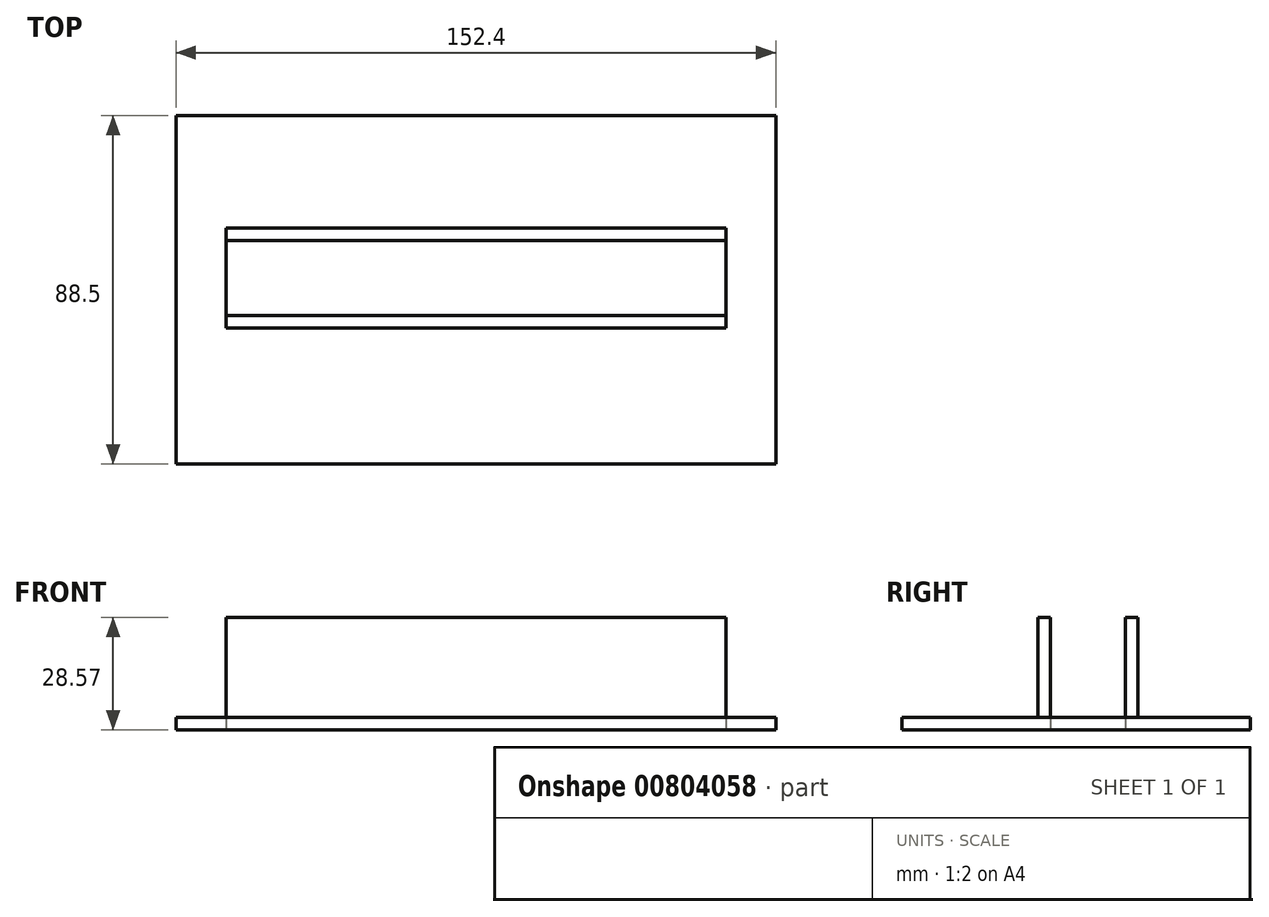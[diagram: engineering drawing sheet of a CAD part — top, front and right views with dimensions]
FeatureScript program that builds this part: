
annotation { "Feature Type Name" : "Feature", "Feature Type Description" : "" }
export const myFeature = defineFeature(function(context is Context, id is Id, definition is map)
    precondition{}
    {
        {
            var Q0;
            Q0=qCreatedBy(makeId("Top.planeOp"),FACE);
            var sketch = newSketch(context, id + "F0", { "sketchPlane" : qUnion([Q0])});
            skLineSegment(sketch, "E0.bottom", {"start": v(-70.99, 5.17) * mm, "end": v(81.41, 5.17) * mm});
            skLineSegment(sketch, "E0.top", {"start": v(-70.99, -83.33) * mm, "end": v(81.41, -83.33) * mm});
            skLineSegment(sketch, "E0.left", {"start": v(-70.99, 5.17) * mm, "end": v(-70.99, -83.33) * mm});
            skLineSegment(sketch, "E0.right", {"start": v(81.41, 5.17) * mm, "end": v(81.41, -83.33) * mm});
            skSolve(sketch);
        }
        {
            var Q0;
            Q0=makeQuery(id+"F0.imprint","IMPRINT",FACE,{"disambiguationData":[TD([[makeQuery(id+"F0.imprint","IMPRINT",EDGE,{"derivedFrom":sQuery(id+"F0.wireOp",EDGE,"E0.bottom")}),-1.0]])]});
            var sketch = newSketch(context, id + "F1", { "sketchPlane" : qUnion([Q0])});
            skLineSegment(sketch, "E1.bottom", {"start": v(-58.29, -45.63) * mm, "end": v(68.71, -45.63) * mm});
            skLineSegment(sketch, "E1.top", {"start": v(-58.29, -26.58) * mm, "end": v(68.71, -26.58) * mm});
            skLineSegment(sketch, "E1.left", {"start": v(-58.29, -45.63) * mm, "end": v(-58.29, -26.58) * mm});
            skLineSegment(sketch, "E1.right", {"start": v(68.71, -45.63) * mm, "end": v(68.71, -26.58) * mm});
            skSolve(sketch);
        }
        {
            var Q0;
            Q0=makeQuery(id+"F1.imprint","IMPRINT",FACE,{"disambiguationData":[TD([[makeQuery(id+"F1.imprint","IMPRINT",EDGE,{"derivedFrom":sQuery(id+"F1.wireOp",EDGE,"E1.bottom")}),-1.0]])]});
            extrude(context, id + "F2", {"entities" : qUnion([Q0]), "depth" : 3.17 * mm, "offsetDistance" : 25.4 * mm});
        }
        {
            var Q0;
            Q0=makeQuery(id+"F2.opExtrude","CAP_FACE",FACE,{"disambiguationData":[OSD([sQuery(id+"F0.wireOp",EDGE,"E0.bottom"),sQuery(id+"F0.wireOp",EDGE,"E0.top"),sQuery(id+"F0.wireOp",EDGE,"E0.left"),sQuery(id+"F0.wireOp",EDGE,"E0.right"),sQuery(id+"F1.wireOp",EDGE,"E1.bottom"),sQuery(id+"F1.wireOp",EDGE,"E1.top"),sQuery(id+"F1.wireOp",EDGE,"E1.left"),sQuery(id+"F1.wireOp",EDGE,"E1.right")])],"isStart":false});
            var sketch = newSketch(context, id + "F3", { "sketchPlane" : qUnion([Q0])});
            skLineSegment(sketch, "E2.bottom", {"start": v(-58.29, -26.58) * mm, "end": v(68.71, -26.58) * mm});
            skLineSegment(sketch, "E2.top", {"start": v(-58.29, -23.4) * mm, "end": v(68.71, -23.4) * mm});
            skLineSegment(sketch, "E2.left", {"start": v(-58.29, -26.58) * mm, "end": v(-58.29, -23.4) * mm});
            skLineSegment(sketch, "E2.right", {"start": v(68.71, -26.58) * mm, "end": v(68.71, -23.4) * mm});
            skLineSegment(sketch, "E3.bottom", {"start": v(-58.29, -45.63) * mm, "end": v(68.71, -45.63) * mm});
            skLineSegment(sketch, "E3.top", {"start": v(-58.29, -48.8) * mm, "end": v(68.71, -48.8) * mm});
            skLineSegment(sketch, "E3.left", {"start": v(-58.29, -45.63) * mm, "end": v(-58.29, -48.8) * mm});
            skLineSegment(sketch, "E3.right", {"start": v(68.71, -45.63) * mm, "end": v(68.71, -48.8) * mm});
            skSolve(sketch);
        }
        {
            var Q0;
            Q0 = qSketchRegion(id + "F3", true);
            extrude(context, id + "F4", {"entities" : qUnion([Q0]), "operationType" : NewBodyOperationType.ADD, "depth" : 25.4 * mm, "offsetDistance" : 25.4 * mm});
        }
    });
